# Revit family: Concept_3
name_source: partatom
category: Specialty Equipment
revit_build: Autodesk Revit 2016 (Build: 20190508_0715(x64)
units: mm (PartAtom-declared; Revit-internal decimal feet)

## family parameters
Always vertical = Yes
Cut with Voids When Loaded = No
OmniClass Number = 23.40.20.21.14
OmniClass Title = Hand and Hair Dryers
Part Type = Normal
Room Calculation Point = No
Round Connector Dimension = Use Diameter
Shared = No
Work Plane-Based = No

## types (1)
- default
    Article number = 01901.S
    Depth = 263 mm
    Height = 295 mm
    Manufacturer = Nofer
    Material = Aluminum 5052-O
    Noise level = 72
    Power input = 1200 W
    Recomended functional pressure = 3 mm  [stored 0.00984252 ft]
    Soap dispenser capacity = 1 mm  [stored 0.00328084 ft]
    Surface finish = Satin
    Utility frequency = 0
    Voltage = 220 V
    Weight = 1.80 kg
    Width = 230 mm

note: [stored X ft] marks values corroborated as IEEE doubles in the binary element streams (Revit-internal decimal feet)
